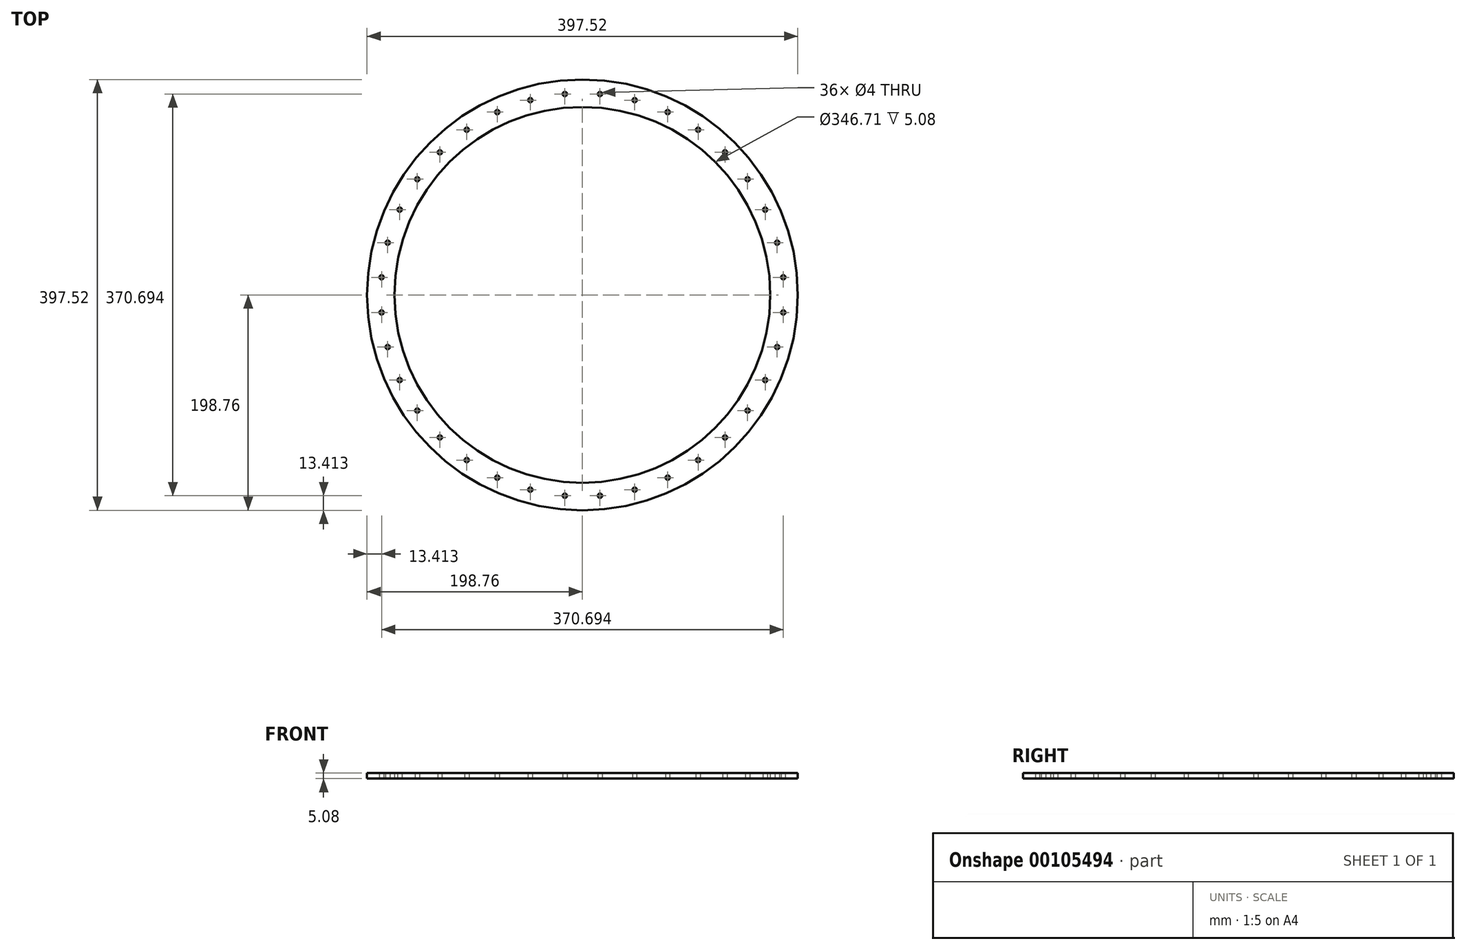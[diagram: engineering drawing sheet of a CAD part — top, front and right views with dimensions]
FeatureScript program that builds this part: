
annotation { "Feature Type Name" : "Feature", "Feature Type Description" : "" }
export const myFeature = defineFeature(function(context is Context, id is Id, definition is map)
    precondition{}
    {
        {
            var Q0;
            Q0=qCreatedBy(makeId("Top.planeOp"),FACE);
            var sketch = newSketch(context, id + "F0", { "sketchPlane" : qUnion([Q0])});
            skCircle(sketch, "E0", {"center": v(0, 0) * mm, "radius": 198.76 * mm});
            skCircle(sketch, "E1", {"center": v(0, 0) * mm, "radius": 173.36 * mm});
            skCircle(sketch, "E2", {"center": v(-16.22, 185.35) * mm, "radius": 2 * mm});
            skCircle(sketch, "E3.1.0", {"center": v(-48.15, 179.72) * mm, "radius": 2 * mm});
            skCircle(sketch, "E3.2.0", {"center": v(-78.63, 168.62) * mm, "radius": 2 * mm});
            skCircle(sketch, "E3.3.0", {"center": v(-106.72, 152.4) * mm, "radius": 2 * mm});
            skCircle(sketch, "E3.4.0", {"center": v(-131.56, 131.56) * mm, "radius": 2 * mm});
            skCircle(sketch, "E3.5.0", {"center": v(-152.4, 106.72) * mm, "radius": 2 * mm});
            skCircle(sketch, "E3.6.0", {"center": v(-168.62, 78.63) * mm, "radius": 2 * mm});
            skCircle(sketch, "E3.7.0", {"center": v(-179.72, 48.15) * mm, "radius": 2 * mm});
            skCircle(sketch, "E3.8.0", {"center": v(-185.35, 16.22) * mm, "radius": 2 * mm});
            skCircle(sketch, "E3.9.0", {"center": v(-185.35, -16.22) * mm, "radius": 2 * mm});
            skCircle(sketch, "E3.10.0", {"center": v(-179.72, -48.15) * mm, "radius": 2 * mm});
            skCircle(sketch, "E3.11.0", {"center": v(-168.62, -78.63) * mm, "radius": 2 * mm});
            skCircle(sketch, "E3.12.0", {"center": v(-152.4, -106.72) * mm, "radius": 2 * mm});
            skCircle(sketch, "E3.13.0", {"center": v(-131.56, -131.56) * mm, "radius": 2 * mm});
            skCircle(sketch, "E3.14.0", {"center": v(-106.72, -152.4) * mm, "radius": 2 * mm});
            skCircle(sketch, "E3.15.0", {"center": v(-78.63, -168.62) * mm, "radius": 2 * mm});
            skCircle(sketch, "E3.16.0", {"center": v(-48.15, -179.72) * mm, "radius": 2 * mm});
            skCircle(sketch, "E3.17.0", {"center": v(-16.22, -185.35) * mm, "radius": 2 * mm});
            skCircle(sketch, "E3.18.0", {"center": v(16.22, -185.35) * mm, "radius": 2 * mm});
            skCircle(sketch, "E3.19.0", {"center": v(48.15, -179.72) * mm, "radius": 2 * mm});
            skCircle(sketch, "E3.20.0", {"center": v(78.63, -168.62) * mm, "radius": 2 * mm});
            skCircle(sketch, "E3.21.0", {"center": v(106.72, -152.4) * mm, "radius": 2 * mm});
            skCircle(sketch, "E3.22.0", {"center": v(131.56, -131.56) * mm, "radius": 2 * mm});
            skCircle(sketch, "E3.23.0", {"center": v(152.4, -106.72) * mm, "radius": 2 * mm});
            skCircle(sketch, "E3.24.0", {"center": v(168.62, -78.63) * mm, "radius": 2 * mm});
            skCircle(sketch, "E3.25.0", {"center": v(179.72, -48.15) * mm, "radius": 2 * mm});
            skCircle(sketch, "E3.26.0", {"center": v(185.35, -16.22) * mm, "radius": 2 * mm});
            skCircle(sketch, "E3.27.0", {"center": v(185.35, 16.22) * mm, "radius": 2 * mm});
            skCircle(sketch, "E3.28.0", {"center": v(179.72, 48.15) * mm, "radius": 2 * mm});
            skCircle(sketch, "E3.29.0", {"center": v(168.62, 78.63) * mm, "radius": 2 * mm});
            skCircle(sketch, "E3.30.0", {"center": v(152.4, 106.72) * mm, "radius": 2 * mm});
            skCircle(sketch, "E3.31.0", {"center": v(131.56, 131.56) * mm, "radius": 2 * mm});
            skCircle(sketch, "E3.32.0", {"center": v(106.72, 152.4) * mm, "radius": 2 * mm});
            skCircle(sketch, "E3.33.0", {"center": v(78.63, 168.62) * mm, "radius": 2 * mm});
            skCircle(sketch, "E3.34.0", {"center": v(48.15, 179.72) * mm, "radius": 2 * mm});
            skCircle(sketch, "E3.35.0", {"center": v(16.22, 185.35) * mm, "radius": 2 * mm});
            skSolve(sketch);
        }
        {
            var Q0;
            Q0 = qSketchRegion(id + "F0", true);
            extrude(context, id + "F1", {"entities" : qUnion([Q0]), "depth" : 5.08 * mm});
        }
    });
